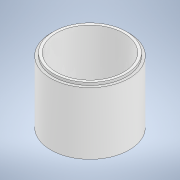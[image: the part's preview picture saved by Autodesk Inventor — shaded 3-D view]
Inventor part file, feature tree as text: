
AUTODESK INVENTOR PART (.ipt)
format: ipt  version: 2020 (Build 240168000, 168)  size: 113,152 bytes
history: native  units: mm
features: extrude x2, sketch x1
ambient origin geometry x8: Origin, YZ Plane, XZ Plane, XY Plane, X Axis, Y Axis, Z Axis, Center Point
bodies: Solid1 (feature_tree)
feature tree (3):
  sketch  "Sketch1"  dims[d0=50.0mm d1=54.0mm d2=58.0mm d3=46.0mm d4=0.0mm d5=44.0mm d6=2.0mm d7=0.0mm d8=0.0mm]
  extrude  "Extrusion1"  Depth=2.0mm
  extrude  "Extrusion2"  Depth=2.0mm
